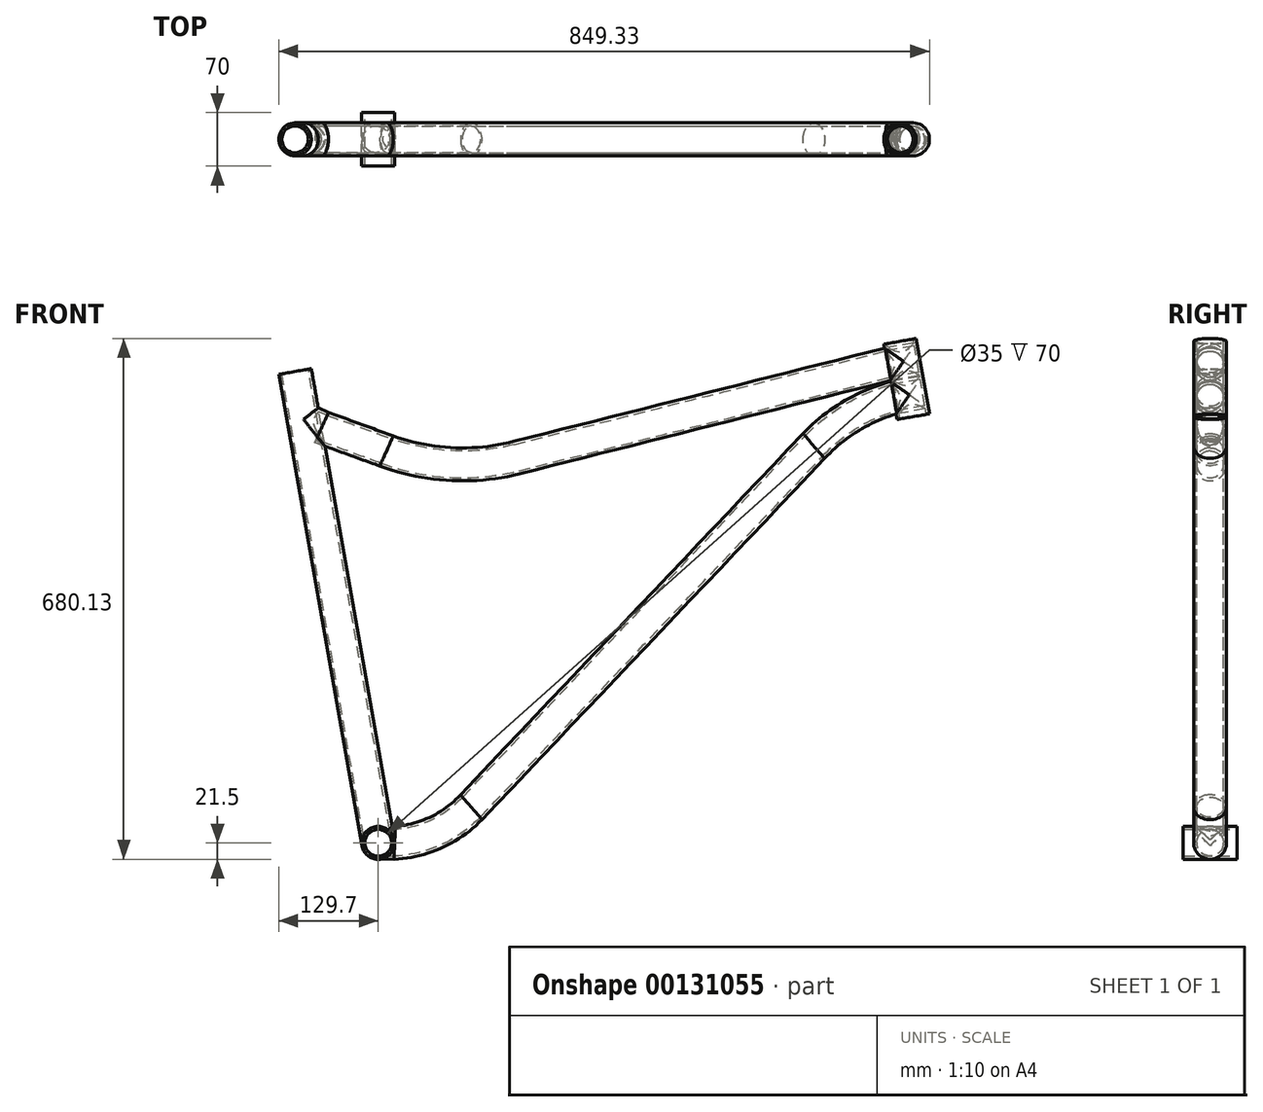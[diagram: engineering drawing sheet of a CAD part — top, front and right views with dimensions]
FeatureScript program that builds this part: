
annotation { "Feature Type Name" : "Feature", "Feature Type Description" : "" }
export const myFeature = defineFeature(function(context is Context, id is Id, definition is map)
    precondition{}
    {
        {
            var Q0;
            Q0=qCreatedBy(makeId("Front.planeOp"),FACE);
            var sketch = newSketch(context, id + "F0", { "sketchPlane" : qUnion([Q0])});
            skCircle(sketch, "E0", {"center": v(0, 0) * mm, "radius": 17.5 * mm});
            skCircle(sketch, "E1", {"center": v(0, 0) * mm, "radius": 21.5 * mm});
            skSolve(sketch);
        }
        {
            var Q0;
            Q0=makeQuery(id+"F0.imprint","IMPRINT",FACE,{"disambiguationData":[TD([[makeQuery(id+"F0.imprint","IMPRINT",EDGE,{"derivedFrom":sQuery(id+"F0.wireOp",EDGE,"E0")}),-1.0]])]});
            extrude(context, id + "F1", {"entities" : qUnion([Q0]), "endBound" : BoundingType.SYMMETRIC, "depth" : 70 * mm});
        }
        {
            var Q0;
            Q0=qCreatedBy(makeId("Top.planeOp"),FACE);
            cPlane(context, id + "F2", {"entities" : qUnion([Q0]), "cplaneType" : CPlaneType.OFFSET, "offset" : 25 * mm, "width" : 150 * mm, "height" : 150 * mm});
        }
        {
            var Q0;
            Q0=qCreatedBy(id+"F2.planeOp",FACE);
            var sketch = newSketch(context, id + "F3", { "sketchPlane" : qUnion([Q0])});
            skCircle(sketch, "E2", {"center": v(0, 0) * mm, "radius": 21.5 * mm});
            skCircle(sketch, "E3", {"center": v(0, 0) * mm, "radius": 17.5 * mm});
            skSolve(sketch);
        }
        {
            var Q0;
            Q0=makeQuery(id+"F3.imprint","IMPRINT",FACE,{"disambiguationData":[TD([[makeQuery(id+"F3.imprint","IMPRINT",EDGE,{"derivedFrom":sQuery(id+"F3.wireOp",EDGE,"E2")}),1.0]])]});
            var Q1;
            Q1=makeQuery(id+"F1.opExtrude","SWEPT_BODY",BODY,{"disambiguationData":[OSD([sQuery(id+"F0.wireOp",EDGE,"E0"),sQuery(id+"F0.wireOp",EDGE,"E1")])]});
            extrude(context, id + "F4", {"entities" : qUnion([Q0]), "operationType" : NewBodyOperationType.ADD, "endBound" : BoundingType.UP_TO_BODY, "oppositeDirection" : true, "endBoundEntityBody" : qUnion([Q1]), "depth" : 25 * mm, "hasSecondDirection" : true, "secondDirectionOppositeDirection" : false, "secondDirectionDepth" : 600 * mm});
        }
        {
            var Q0;
            Q0=qCreatedBy(makeId("Top.planeOp"),FACE);
            var sketch = newSketch(context, id + "F5", { "sketchPlane" : qUnion([Q0])});
            skLineSegment(sketch, "E4", {"start": v(0, 0) * mm, "end": v(0, -25.35) * mm, "construction": true});
            skSolve(sketch);
        }
        {
            var Q0;
            Q0=makeQuery(id+"F1.opExtrude","SWEPT_BODY",BODY,{"disambiguationData":[OSD([sQuery(id+"F0.wireOp",EDGE,"E0"),sQuery(id+"F0.wireOp",EDGE,"E1")])]});
            var Q1;
            Q1=sQuery(id+"F5.wireOp",EDGE,"E4");
            var Q2;
            Q2=sQuery(id+"F5.wireOp",EDGE,"E4");
            transform(context, id + "F6", {"entities" : qUnion([Q0]), "transformType" : TransformType.ROTATION, "transformAxis" : qUnion([Q2]), "angle" : 10 * degree, "makeCopy" : false});
        }
        {
            var Q0;
            Q0=qCreatedBy(makeId("Front.planeOp"),FACE);
            var sketch = newSketch(context, id + "F7", { "sketchPlane" : qUnion([Q0])});
            skLineSegment(sketch, "E5", {"start": v(-87.36, 619.24) * mm, "end": v(21.17, 3.73) * mm});
            skLineSegment(sketch, "E6", {"start": v(-73.82, 542.45) * mm, "end": v(10.76, 511.67) * mm});
            skLineSegment(sketch, "E7", {"start": v(180.76, 502.96) * mm, "end": v(665.62, 625.05) * mm});
            skArc(sketch, "E8", {"start": v(10.76, 511.67) * mm, "mid": v(95.1, 494.56) * mm, "end": v(180.76, 502.96) * mm});
            skSolve(sketch);
        }
        {
            var Q0;
            Q0=sQuery(id+"F7.wireOp",EDGE,"E5");
            var Q1;
            Q1=sQuery(id+"F7.wireOp",VERTEX,"E7.end");
            cPlane(context, id + "F8", {"entities" : qUnion([Q0, Q1]), "cplaneType" : CPlaneType.LINE_POINT, "offset" : 25 * mm, "width" : 150 * mm, "height" : 150 * mm});
        }
        {
            var Q0;
            Q0=qCreatedBy(id+"F8.planeOp",FACE);
            var sketch = newSketch(context, id + "F9", { "sketchPlane" : qUnion([Q0])});
            skPoint(sketch, "E9.0", {"position": v(764.05, 0) * mm});
            skLineSegment(sketch, "E10", {"start": v(764.05, 0) * mm, "end": v(764.05, 26.4) * mm, "construction": true});
            skSolve(sketch);
        }
        {
            var Q0;
            Q0=qCreatedBy(id+"F8.planeOp",FACE);
            var Q1;
            Q1=sQuery(id+"F9.wireOp",EDGE,"E10");
            cPlane(context, id + "F10", {"entities" : qUnion([Q0, Q1]), "cplaneType" : CPlaneType.LINE_ANGLE, "offset" : 25 * mm, "angle" : 90 * degree, "width" : 150 * mm, "height" : 150 * mm});
        }
        {
            var Q0;
            Q0=qCreatedBy(id+"F10.planeOp",FACE);
            var sketch = newSketch(context, id + "F11", { "sketchPlane" : qUnion([Q0])});
            skPoint(sketch, "E11.0", {"position": v(0, 499.97) * mm});
            skCircle(sketch, "E12", {"center": v(0, 499.97) * mm, "radius": 21.5 * mm});
            skCircle(sketch, "E13", {"center": v(0, 499.97) * mm, "radius": 17.5 * mm});
            skLineSegment(sketch, "E14", {"start": v(0, 499.97) * mm, "end": v(0, 427.93) * mm, "construction": true});
            skCircle(sketch, "E15", {"center": v(0, 455.62) * mm, "radius": 21.5 * mm});
            skCircle(sketch, "E16", {"center": v(0, 455.62) * mm, "radius": 17.5 * mm});
            skSolve(sketch);
        }
        {
            var Q0;
            Q0=makeQuery(id+"F11.imprint","IMPRINT",FACE,{"disambiguationData":[TD([[makeQuery(id+"F11.imprint","IMPRINT",EDGE,{"derivedFrom":sQuery(id+"F11.wireOp",EDGE,"E12")}),1.0]])]});
            var Q1;
            Q1=sQuery(id+"F7.wireOp",EDGE,"E7");
            var Q2;
            Q2=sQuery(id+"F7.wireOp",EDGE,"E8");
            var Q3;
            Q3=sQuery(id+"F7.wireOp",EDGE,"E6");
            sweep(context, id + "F12", {"operationType" : NewBodyOperationType.ADD, "profiles" : qUnion([Q0]), "path" : qUnion([Q1, Q2, Q3])});
        }
        {
            var Q0;
            {var subQ0=sQuery(id+"F11.wireOp",EDGE,"E12");var subQ2=sQuery(id+"F11.wireOp",EDGE,"E13");Q0=makeQuery(id+"F12.boolean.opBoolean","SPLIT",FACE,{"disambiguationData":[TD([makeQuery(id+"F4.opExtrude","SWEPT_FACE",FACE,{"disambiguationData":[OSD([sQuery(id+"F3.wireOp",EDGE,"E2")])]})])],"derivedFrom":makeQuery(id+"F12.opSweep","CAP_FACE",FACE,{"disambiguationData":[OSD([sQuery(id+"F7.wireOp",VERTEX,"E6.start"),subQ0,subQ2])],"isStart":false})});}
            var Q1;
            Q1=makeQuery(id+"F1.opExtrude","SWEPT_BODY",BODY,{"disambiguationData":[OSD([sQuery(id+"F0.wireOp",EDGE,"E0"),sQuery(id+"F0.wireOp",EDGE,"E1")])]});
            extrude(context, id + "F13", {"entities" : qUnion([Q0]), "operationType" : NewBodyOperationType.ADD, "endBound" : BoundingType.UP_TO_BODY, "endBoundEntityBody" : qUnion([Q1]), "depth" : 25 * mm});
        }
        {
            var Q0;
            Q0=qCreatedBy(makeId("Front.planeOp"),FACE);
            var sketch = newSketch(context, id + "F14", { "sketchPlane" : qUnion([Q0])});
            skPoint(sketch, "E17.0", {"position": v(673.32, 581.38) * mm});
            skLineSegment(sketch, "E18", {"start": v(568.73, 518.22) * mm, "end": v(121.5, 46.53) * mm});
            skArc(sketch, "E19", {"start": v(673.32, 581.38) * mm, "mid": v(616.75, 556.87) * mm, "end": v(568.73, 518.22) * mm});
            skCircle(sketch, "E20.0", {"center": v(0, 0) * mm, "radius": 21.5 * mm});
            skArc(sketch, "E21", {"start": v(21.5, 0) * mm, "mid": v(75.93, 13.74) * mm, "end": v(121.5, 46.53) * mm});
            skSolve(sketch);
        }
        {
            var Q0;
            Q0=makeQuery(id+"F11.imprint","IMPRINT",FACE,{"disambiguationData":[TD([[makeQuery(id+"F11.imprint","IMPRINT",EDGE,{"derivedFrom":sQuery(id+"F11.wireOp",EDGE,"E15")}),1.0]])]});
            var Q1;
            Q1=sQuery(id+"F14.wireOp",EDGE,"E19");
            var Q2;
            Q2=sQuery(id+"F14.wireOp",EDGE,"E18");
            var Q3;
            Q3=sQuery(id+"F14.wireOp",EDGE,"E21");
            sweep(context, id + "F15", {"operationType" : NewBodyOperationType.ADD, "profiles" : qUnion([Q0]), "path" : qUnion([Q1, Q2, Q3])});
        }
        {
            var Q0;
            Q0=makeQuery(id+"F15.boolean.opBoolean","SPLIT",FACE,{"disambiguationData":[OD(0.0)],"derivedFrom":makeQuery(id+"F15.opSweep","CAP_FACE",FACE,{"disambiguationData":[OSD([sQuery(id+"F11.wireOp",EDGE,"E15"),sQuery(id+"F11.wireOp",EDGE,"E16"),sQuery(id+"F14.wireOp",VERTEX,"E21.start")])],"isStart":false})});
            var Q1;
            Q1=makeQuery(id+"F15.boolean.opBoolean","SPLIT",FACE,{"disambiguationData":[OD(1.0)],"derivedFrom":makeQuery(id+"F15.opSweep","CAP_FACE",FACE,{"disambiguationData":[OSD([sQuery(id+"F11.wireOp",EDGE,"E15"),sQuery(id+"F11.wireOp",EDGE,"E16"),sQuery(id+"F14.wireOp",VERTEX,"E21.start")])],"isStart":false})});
            var Q2;
            Q2=makeQuery(id+"F1.opExtrude","SWEPT_BODY",BODY,{"disambiguationData":[OSD([sQuery(id+"F0.wireOp",EDGE,"E0"),sQuery(id+"F0.wireOp",EDGE,"E1")])]});
            extrude(context, id + "F16", {"entities" : qUnion([Q0, Q1]), "operationType" : NewBodyOperationType.ADD, "endBound" : BoundingType.UP_TO_BODY, "endBoundEntityBody" : qUnion([Q2]), "depth" : 25 * mm});
        }
        {
            var Q0;
            Q0=qCreatedBy(id+"F8.planeOp",FACE);
            var sketch = newSketch(context, id + "F17", { "sketchPlane" : qUnion([Q0])});
            skPoint(sketch, "E22.0", {"position": v(764.05, 0) * mm});
            skLineSegment(sketch, "E23", {"start": v(764.05, 0) * mm, "end": v(810.74, 0) * mm, "construction": true});
            skCircle(sketch, "E24", {"center": v(784.49, 0) * mm, "radius": 21.5 * mm});
            skCircle(sketch, "E25", {"center": v(784.49, 0) * mm, "radius": 17.5 * mm});
            skLineSegment(sketch, "E26", {"start": v(762.99, 0) * mm, "end": v(764.05, 0) * mm});
            skSolve(sketch);
        }
        {
            var Q0;
            Q0 = qSketchRegion(id + "F17", true);
            extrude(context, id + "F18", {"entities" : qUnion([Q0]), "operationType" : NewBodyOperationType.ADD, "depth" : 73.2 * mm, "hasSecondDirection" : true, "secondDirectionOppositeDirection" : true, "secondDirectionDepth" : 26.7 * mm});
        }
        {
            var Q0;
            Q0=makeQuery(id+"F11.imprint","IMPRINT",FACE,{"disambiguationData":[TD([[makeQuery(id+"F11.imprint","IMPRINT",EDGE,{"derivedFrom":sQuery(id+"F11.wireOp",EDGE,"E12")}),1.0]])]});
            var Q1;
            Q1=makeQuery(id+"F11.imprint","IMPRINT",FACE,{"disambiguationData":[TD([[makeQuery(id+"F11.imprint","IMPRINT",EDGE,{"derivedFrom":sQuery(id+"F11.wireOp",EDGE,"E15")}),1.0]])]});
            var Q2;
            Q2=makeQuery(id+"F18.opExtrude","SWEPT_FACE",FACE,{"disambiguationData":[OSD([sQuery(id+"F17.wireOp",EDGE,"E24")])]});
            var Q3;
            Q3=makeQuery(id+"F1.opExtrude","SWEPT_BODY",BODY,{"disambiguationData":[OSD([sQuery(id+"F0.wireOp",EDGE,"E0"),sQuery(id+"F0.wireOp",EDGE,"E1")])]});
            extrude(context, id + "F19", {"entities" : qUnion([Q0, Q1]), "operationType" : NewBodyOperationType.ADD, "endBound" : BoundingType.UP_TO_SURFACE, "oppositeDirection" : true, "endBoundEntityFace" : qUnion([Q2]), "endBoundEntityBody" : qUnion([Q3]), "depth" : 25 * mm});
        }
    });
